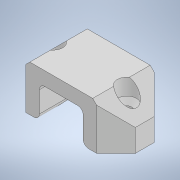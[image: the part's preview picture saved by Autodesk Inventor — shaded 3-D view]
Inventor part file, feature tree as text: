
AUTODESK INVENTOR PART (.ipt)
format: ipt  version: 2022 (Build 260153000, 153)  size: 216,064 bytes
history: native  units: mm
features: projected_geometry x6, sketch x5, extrude x4, chamfer x2, thicken_offset x2, plane x1, hole x1, fillet x1
ambient origin geometry x8: Origin, YZ Plane, XZ Plane, XY Plane, X Axis, Y Axis, Z Axis, Center Point
bodies: Solid1 (feature_tree)
feature tree (22):
  extrude  "Extrusion1"  Depth=16.0mm
  plane  "Work Plane1"
  extrude  "Extrusion3"  Depth=12.0mm
  hole  "Hole1"  [1 undecoded]
  fillet  "Fillet1"  [1 undecoded]
  extrude  "Extrusion4"  Depth=8.0mm
  chamfer  "Chamfer2"  Distance=3.0mm Angle=30.0deg
  extrude  "Extrusion5"  Depth=2.0mm
  thicken_offset  "Thicken1"
  thicken_offset  "Thicken2"
  chamfer  "Chamfer3"  Distance=7.0mm
  sketch  "Sketch1"  dims[d0=11.7mm d1=16.0mm]
  sketch  "Sketch3"  dims[d2=12.0mm d3=12.0mm]
  projected_geometry  "Projected Loop3"
  projected_geometry  "Projected Loop4"
  sketch  "Sketch4"  dims[d4=5.0mm d5=21.0mm d6=0.0mm d12=-3.0mm]
  projected_geometry  "Projected Loop5"
  projected_geometry  "Projected Loop6"
  sketch  "Sketch5"  dims[d13=8.0mm d14=8.0mm]
  projected_geometry  "Projected Loop7"
  sketch  "Sketch6"  dims[d15=27.0mm d16=3.0mm d17=30.0deg d18=3.4mm d19=6.0mm d20=6.3mm d21=2.0mm d22=90.0deg d23=8.0mm d24=0.0mm d28=2.0mm d29=7.0mm d30=6.0mm d31=0.0mm d32=1.8mm d33=2.0mm d34=45.0deg d35=135.0deg d36=45.0deg d37=5.0mm d38=0.0mm d39=0.0mm d40=0.2mm d41=0.2mm d42=0.2mm d43=0.2mm d44=8.5mm d45=2.0mm d46=45.0deg]
  projected_geometry  "Projected Loop8"
note: 2 required parameter values undecoded (feature->parameter linkage not recoverable at this tier; creation-order binding heuristic only, values carry confidence <= 0.55)
